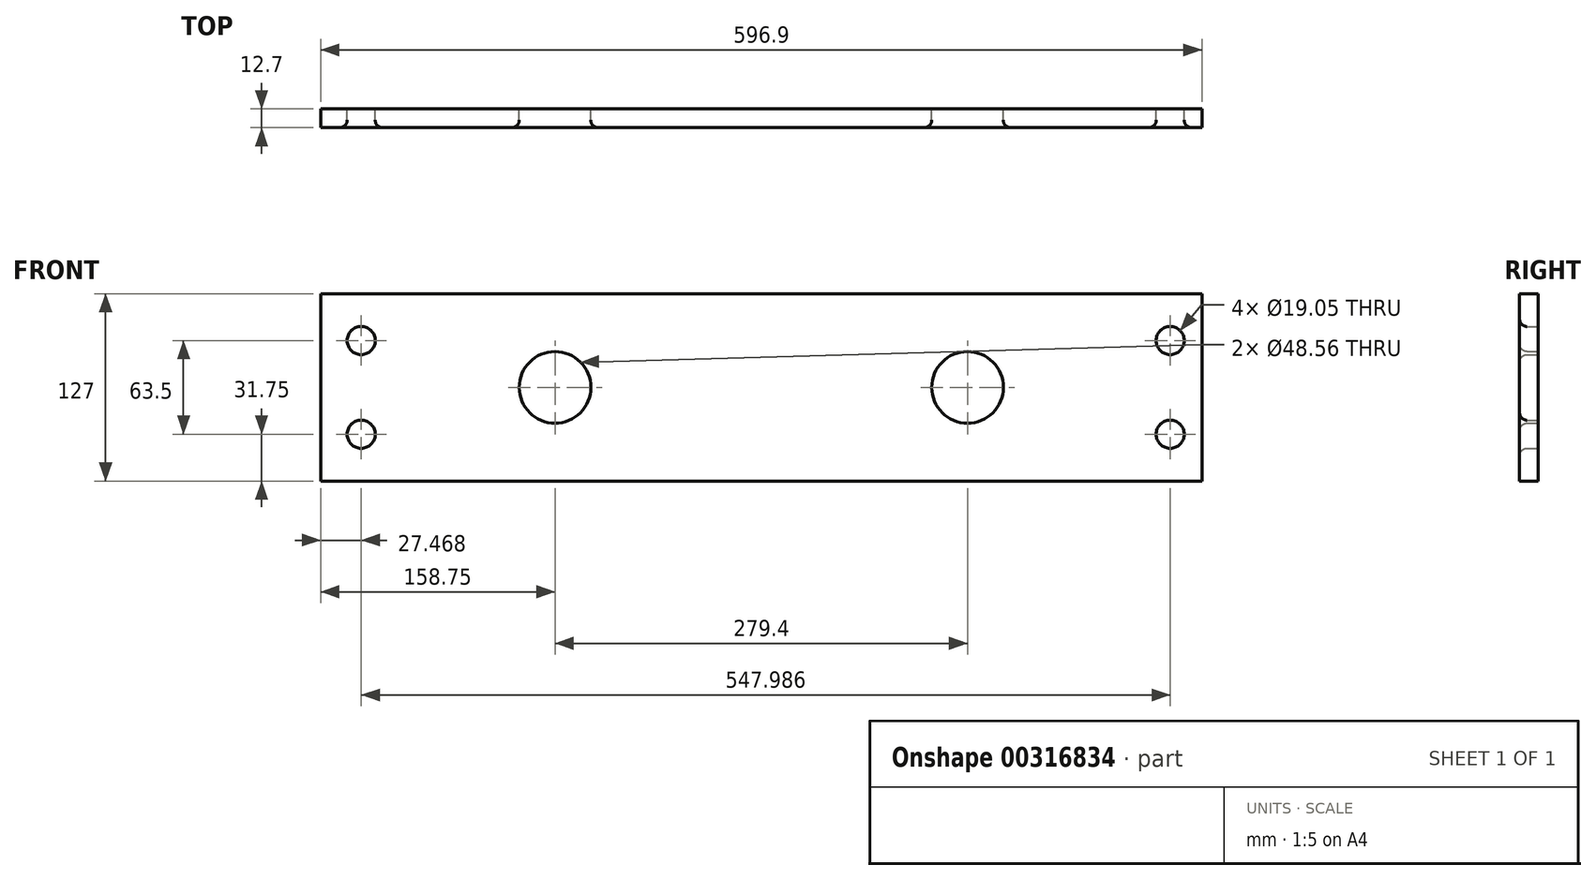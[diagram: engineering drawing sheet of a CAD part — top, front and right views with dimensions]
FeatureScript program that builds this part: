
annotation { "Feature Type Name" : "Feature", "Feature Type Description" : "" }
export const myFeature = defineFeature(function(context is Context, id is Id, definition is map)
    precondition{}
    {
        {
            var Q0;
            Q0=qCreatedBy(makeId("Front.planeOp"),FACE);
            var sketch = newSketch(context, id + "F0", { "sketchPlane" : qUnion([Q0])});
            skLineSegment(sketch, "E0.bottom", {"start": v(298.45, -63.5) * mm, "end": v(-298.45, -63.5) * mm});
            skLineSegment(sketch, "E0.top", {"start": v(298.45, 63.5) * mm, "end": v(-298.45, 63.5) * mm});
            skLineSegment(sketch, "E0.left", {"start": v(298.45, -63.5) * mm, "end": v(298.45, 63.5) * mm});
            skLineSegment(sketch, "E0.right", {"start": v(-298.45, -63.5) * mm, "end": v(-298.45, 63.5) * mm});
            skPoint(sketch, "E0.middle", {"position": v(0, 0) * mm});
            skLineSegment(sketch, "E1", {"start": v(-298.45, 31.75) * mm, "end": v(298.45, 31.75) * mm, "construction": true});
            skLineSegment(sketch, "E2", {"start": v(298.45, 0) * mm, "end": v(-298.45, 0) * mm, "construction": true});
            skLineSegment(sketch, "E3", {"start": v(-298.45, -31.75) * mm, "end": v(298.45, -31.75) * mm, "construction": true});
            skCircle(sketch, "E4", {"center": v(-139.7, 0) * mm, "radius": 24.28 * mm});
            skCircle(sketch, "E5", {"center": v(139.7, 0) * mm, "radius": 24.28 * mm});
            skCircle(sketch, "E6", {"center": v(277, 31.75) * mm, "radius": 9.53 * mm});
            skCircle(sketch, "E7", {"center": v(277, -31.75) * mm, "radius": 9.53 * mm});
            skCircle(sketch, "E8", {"center": v(-270.98, -31.75) * mm, "radius": 9.53 * mm});
            skCircle(sketch, "E9", {"center": v(-270.98, 31.75) * mm, "radius": 9.53 * mm});
            skSolve(sketch);
        }
        {
            var Q0;
            Q0=makeQuery(id+"F0.imprint","IMPRINT",FACE,{"disambiguationData":[TD([[makeQuery(id+"F0.imprint","IMPRINT",EDGE,{"derivedFrom":sQuery(id+"F0.wireOp",EDGE,"E0.bottom")}),-1.0]])]});
            extrude(context, id + "F1", {"entities" : qUnion([Q0]), "depth" : 12.7 * mm});
        }
        {
            var Q0;
            Q0=makeQuery(id+"F1.opExtrude","CAP_EDGE",EDGE,{"disambiguationData":[OSD([sQuery(id+"F0.wireOp",EDGE,"E4")])],"isStart":false});
            var Q1;
            Q1=makeQuery(id+"F1.opExtrude","CAP_EDGE",EDGE,{"disambiguationData":[OSD([sQuery(id+"F0.wireOp",EDGE,"E9")])],"isStart":false});
            var Q2;
            Q2=makeQuery(id+"F1.opExtrude","CAP_EDGE",EDGE,{"disambiguationData":[OSD([sQuery(id+"F0.wireOp",EDGE,"E8")])],"isStart":false});
            var Q3;
            Q3=makeQuery(id+"F1.opExtrude","CAP_EDGE",EDGE,{"disambiguationData":[OSD([sQuery(id+"F0.wireOp",EDGE,"E5")])],"isStart":false});
            var Q4;
            Q4=makeQuery(id+"F1.opExtrude","CAP_EDGE",EDGE,{"disambiguationData":[OSD([sQuery(id+"F0.wireOp",EDGE,"E7")])],"isStart":false});
            var Q5;
            Q5=makeQuery(id+"F1.opExtrude","CAP_EDGE",EDGE,{"disambiguationData":[OSD([sQuery(id+"F0.wireOp",EDGE,"E6")])],"isStart":false});
            fillet(context, id + "F2", {"entities" : qUnion([Q0, Q1, Q2, Q3, Q4, Q5]), "radius" : 5.08 * mm, "tangentPropagation" : true, "allowEdgeOverflow" : false});
        }
    });
